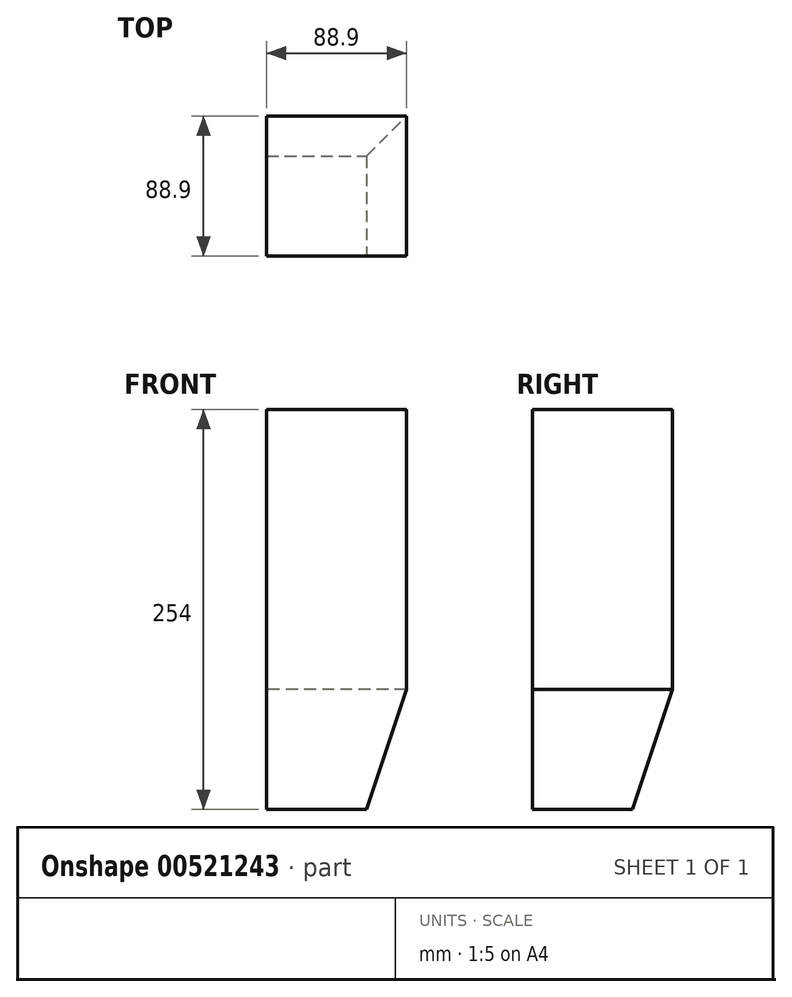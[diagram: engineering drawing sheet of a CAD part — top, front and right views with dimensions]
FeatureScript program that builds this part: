
annotation { "Feature Type Name" : "Feature", "Feature Type Description" : "" }
export const myFeature = defineFeature(function(context is Context, id is Id, definition is map)
    precondition{}
    {
        {
            var Q0;
            Q0=qCreatedBy(makeId("Top.planeOp"),FACE);
            var sketch = newSketch(context, id + "F0", { "sketchPlane" : qUnion([Q0])});
            skLineSegment(sketch, "E0.bottom", {"start": v(-44.45, 44.45) * mm, "end": v(44.45, 44.45) * mm});
            skLineSegment(sketch, "E0.top", {"start": v(-44.45, -44.45) * mm, "end": v(44.45, -44.45) * mm});
            skLineSegment(sketch, "E0.left", {"start": v(-44.45, 44.45) * mm, "end": v(-44.45, -44.45) * mm});
            skLineSegment(sketch, "E0.right", {"start": v(44.45, 44.45) * mm, "end": v(44.45, -44.45) * mm});
            skLineSegment(sketch, "E1", {"start": v(0, 50.94) * mm, "end": v(0, -48.13) * mm});
            skLineSegment(sketch, "E2", {"start": v(63.09, 0) * mm, "end": v(-58.02, 0) * mm});
            skSolve(sketch);
        }
        {
            var Q0;
            {var subQ0=sQuery(id+"F0.wireOp",EDGE,"E0.left");var subQ1=sQuery(id+"F0.wireOp",EDGE,"E0.bottom");var subQ2=makeQuery(id+"F0.imprint","INTERSECT",VERTEX,{"derivedFrom":[subQ1,subQ0]});Q0=makeQuery(id+"F0.imprint","IMPRINT",FACE,{"disambiguationData":[TD([[makeQuery(id+"F0.imprint","IMPRINT",EDGE,{"disambiguationData":[TD([[subQ2,-1.0]])],"derivedFrom":subQ1}),-1.0]])]});}
            var Q1;
            {var subQ0=sQuery(id+"F0.wireOp",EDGE,"E0.right");var subQ1=sQuery(id+"F0.wireOp",EDGE,"E0.bottom");var subQ2=makeQuery(id+"F0.imprint","INTERSECT",VERTEX,{"derivedFrom":[subQ1,subQ0]});Q1=makeQuery(id+"F0.imprint","IMPRINT",FACE,{"disambiguationData":[TD([[makeQuery(id+"F0.imprint","IMPRINT",EDGE,{"disambiguationData":[TD([[subQ2,1.0]])],"derivedFrom":subQ1}),-1.0]])]});}
            var Q2;
            {var subQ0=sQuery(id+"F0.wireOp",EDGE,"E0.right");var subQ1=sQuery(id+"F0.wireOp",EDGE,"E0.top");var subQ2=makeQuery(id+"F0.imprint","INTERSECT",VERTEX,{"derivedFrom":[subQ1,subQ0]});Q2=makeQuery(id+"F0.imprint","IMPRINT",FACE,{"disambiguationData":[TD([[makeQuery(id+"F0.imprint","IMPRINT",EDGE,{"disambiguationData":[TD([[subQ2,1.0]])],"derivedFrom":subQ1}),1.0]])]});}
            var Q3;
            {var subQ0=sQuery(id+"F0.wireOp",EDGE,"E0.left");var subQ1=sQuery(id+"F0.wireOp",EDGE,"E0.top");var subQ2=makeQuery(id+"F0.imprint","INTERSECT",VERTEX,{"derivedFrom":[subQ1,subQ0]});Q3=makeQuery(id+"F0.imprint","IMPRINT",FACE,{"disambiguationData":[TD([[makeQuery(id+"F0.imprint","IMPRINT",EDGE,{"disambiguationData":[TD([[subQ2,-1.0]])],"derivedFrom":subQ1}),1.0]])]});}
            extrude(context, id + "F1", {"entities" : qUnion([Q0, Q1, Q2, Q3]), "depth" : 254 * mm, "offsetDistance" : 25.4 * mm});
        }
        {
            var Q0;
            Q0=makeQuery(id+"F1.opExtrude","CAP_EDGE",EDGE,{"disambiguationData":[OSD([sQuery(id+"F0.wireOp",EDGE,"E0.right")])],"isStart":true});
            chamfer(context, id + "F2", {"entities" : qUnion([Q0]), "chamferType" : ChamferType.TWO_OFFSETS, "width1" : 25.4 * mm, "oppositeDirection" : false, "width2" : 76.2 * mm, "tangentPropagation" : true});
        }
        {
            var Q0;
            Q0=makeQuery(id+"F1.opExtrude","CAP_EDGE",EDGE,{"disambiguationData":[OSD([sQuery(id+"F0.wireOp",EDGE,"E0.bottom")])],"isStart":true});
            chamfer(context, id + "F3", {"entities" : qUnion([Q0]), "chamferType" : ChamferType.TWO_OFFSETS, "width1" : 25.4 * mm, "oppositeDirection" : false, "width2" : 76.2 * mm, "tangentPropagation" : true});
        }
    });
